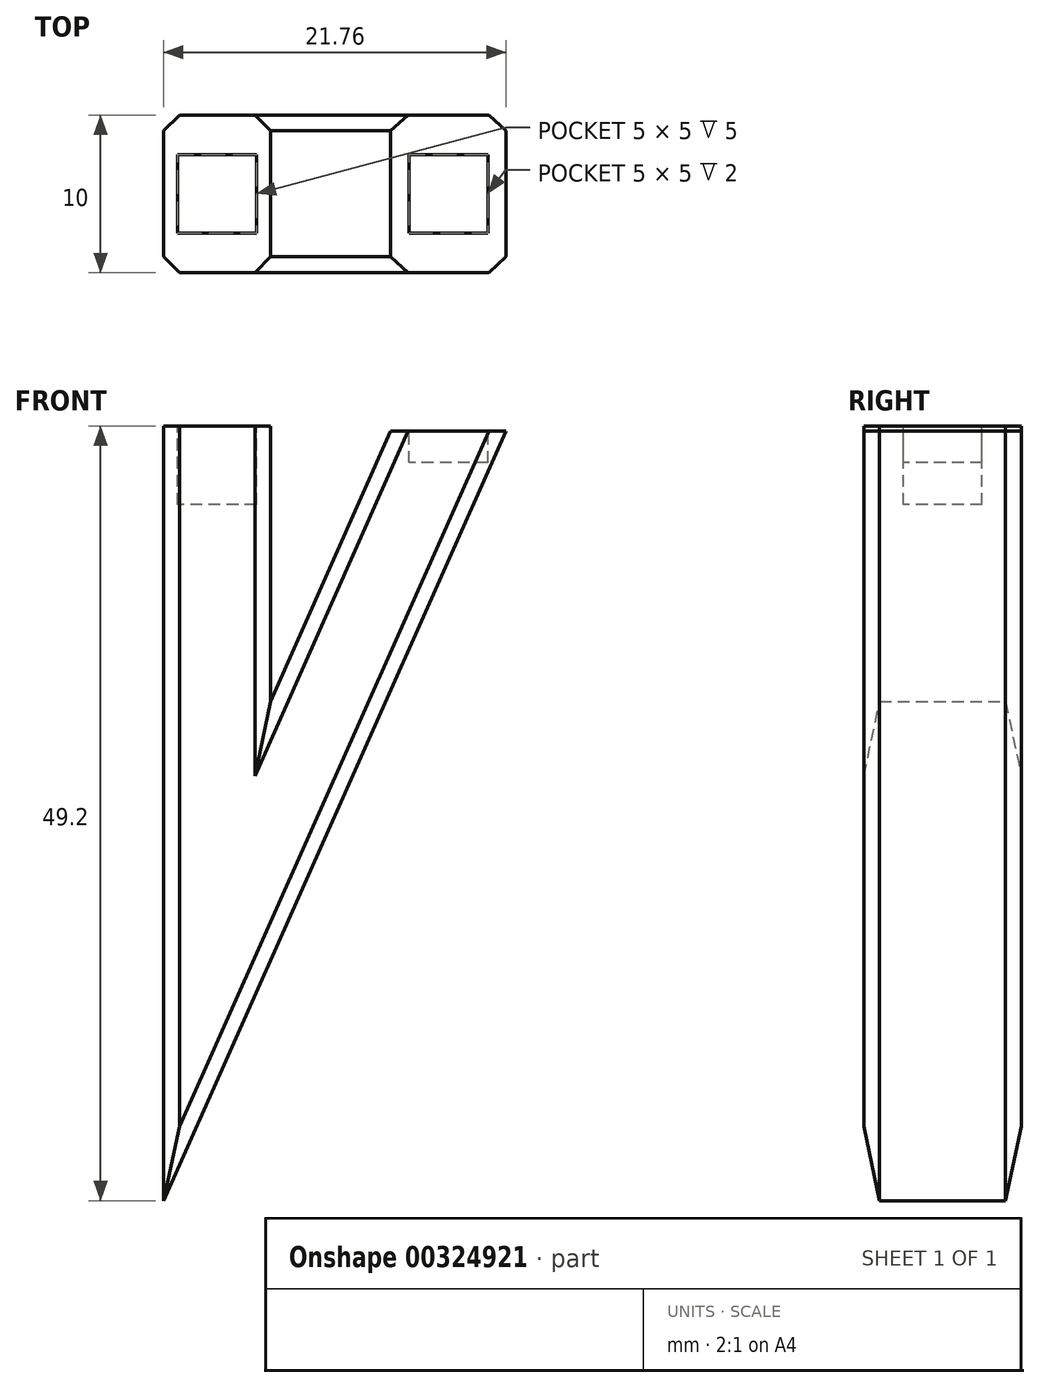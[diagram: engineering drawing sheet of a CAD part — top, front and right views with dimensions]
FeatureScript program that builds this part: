
annotation { "Feature Type Name" : "Feature", "Feature Type Description" : "" }
export const myFeature = defineFeature(function(context is Context, id is Id, definition is map)
    precondition{}
    {
        {
            var Q0;
            Q0=qCreatedBy(makeId("Front.planeOp"),FACE);
            var sketch = newSketch(context, id + "F0", { "sketchPlane" : qUnion([Q0])});
            skLineSegment(sketch, "E0", {"start": v(0, 0) * mm, "end": v(0, 49.2) * mm});
            skLineSegment(sketch, "E1", {"start": v(0, 0) * mm, "end": v(21.76, 48.87) * mm});
            skLineSegment(sketch, "E2", {"start": v(0, 49.2) * mm, "end": v(6.8, 49.2) * mm});
            skLineSegment(sketch, "E3", {"start": v(21.76, 48.87) * mm, "end": v(14.42, 48.87) * mm});
            skLineSegment(sketch, "E4", {"start": v(6.8, 49.2) * mm, "end": v(6.8, 31.7) * mm});
            skLineSegment(sketch, "E5", {"start": v(14.42, 48.87) * mm, "end": v(6.8, 31.7) * mm});
            skSolve(sketch);
        }
        {
            var Q0;
            Q0=makeQuery(id+"F0.imprint","IMPRINT",FACE,{"disambiguationData":[TD([[makeQuery(id+"F0.imprint","IMPRINT",EDGE,{"derivedFrom":sQuery(id+"F0.wireOp",EDGE,"E0")}),-1.0]])]});
            extrude(context, id + "F1", {"entities" : qUnion([Q0]), "depth" : 10 * mm});
        }
        {
            var Q0;
            Q0=makeQuery(id+"F1.opExtrude","SWEPT_FACE",FACE,{"disambiguationData":[OSD([sQuery(id+"F0.wireOp",EDGE,"E2")])]});
            var sketch = newSketch(context, id + "F2", { "sketchPlane" : qUnion([Q0])});
            skLineSegment(sketch, "E6.bottom", {"start": v(5.9, -2.5) * mm, "end": v(0.9, -2.5) * mm});
            skLineSegment(sketch, "E6.top", {"start": v(5.9, -7.5) * mm, "end": v(0.9, -7.5) * mm});
            skLineSegment(sketch, "E6.left", {"start": v(5.9, -2.5) * mm, "end": v(5.9, -7.5) * mm});
            skLineSegment(sketch, "E6.right", {"start": v(0.9, -2.5) * mm, "end": v(0.9, -7.5) * mm});
            skPoint(sketch, "E6.middle", {"position": v(3.4, -5) * mm});
            skSolve(sketch);
        }
        {
            var Q0;
            Q0=makeQuery(id+"F2.imprint","IMPRINT",FACE,{"disambiguationData":[TD([[makeQuery(id+"F2.imprint","IMPRINT",EDGE,{"derivedFrom":sQuery(id+"F2.wireOp",EDGE,"E6.bottom")}),1.0]])]});
            extrude(context, id + "F3", {"entities" : qUnion([Q0]), "operationType" : NewBodyOperationType.REMOVE, "oppositeDirection" : true, "depth" : 5 * mm});
        }
        {
            var Q0;
            Q0=makeQuery(id+"F1.opExtrude","SWEPT_FACE",FACE,{"disambiguationData":[OSD([sQuery(id+"F0.wireOp",EDGE,"E3")])]});
            var sketch = newSketch(context, id + "F4", { "sketchPlane" : qUnion([Q0])});
            skLineSegment(sketch, "E7.bottom", {"start": v(20.6, -2.5) * mm, "end": v(15.6, -2.5) * mm});
            skLineSegment(sketch, "E7.top", {"start": v(20.6, -7.5) * mm, "end": v(15.6, -7.5) * mm});
            skLineSegment(sketch, "E7.left", {"start": v(20.6, -2.5) * mm, "end": v(20.6, -7.5) * mm});
            skLineSegment(sketch, "E7.right", {"start": v(15.6, -2.5) * mm, "end": v(15.6, -7.5) * mm});
            skPoint(sketch, "E7.middle", {"position": v(18.1, -5) * mm});
            skSolve(sketch);
        }
        {
            var Q0;
            Q0=makeQuery(id+"F4.imprint","IMPRINT",FACE,{"disambiguationData":[TD([[makeQuery(id+"F4.imprint","IMPRINT",EDGE,{"derivedFrom":sQuery(id+"F4.wireOp",EDGE,"E7.bottom")}),1.0]])]});
            extrude(context, id + "F5", {"entities" : qUnion([Q0]), "operationType" : NewBodyOperationType.REMOVE, "oppositeDirection" : true, "depth" : 2 * mm});
        }
        {
            var Q0;
            Q0=makeQuery(id+"F1.opExtrude","CAP_EDGE",EDGE,{"disambiguationData":[OSD([sQuery(id+"F0.wireOp",EDGE,"E4")])],"isStart":false});
            var Q1;
            Q1=makeQuery(id+"F1.opExtrude","CAP_EDGE",EDGE,{"disambiguationData":[OSD([sQuery(id+"F0.wireOp",EDGE,"E0")])],"isStart":false});
            var Q2;
            Q2=makeQuery(id+"F1.opExtrude","CAP_EDGE",EDGE,{"disambiguationData":[OSD([sQuery(id+"F0.wireOp",EDGE,"E5")])],"isStart":false});
            var Q3;
            Q3=makeQuery(id+"F1.opExtrude","CAP_EDGE",EDGE,{"disambiguationData":[OSD([sQuery(id+"F0.wireOp",EDGE,"E4")])],"isStart":true});
            var Q4;
            Q4=makeQuery(id+"F1.opExtrude","CAP_EDGE",EDGE,{"disambiguationData":[OSD([sQuery(id+"F0.wireOp",EDGE,"E1")])],"isStart":true});
            var Q5;
            Q5=makeQuery(id+"F1.opExtrude","CAP_EDGE",EDGE,{"disambiguationData":[OSD([sQuery(id+"F0.wireOp",EDGE,"E5")])],"isStart":true});
            var Q6;
            Q6=makeQuery(id+"F1.opExtrude","CAP_EDGE",EDGE,{"disambiguationData":[OSD([sQuery(id+"F0.wireOp",EDGE,"E1")])],"isStart":false});
            var Q7;
            Q7=makeQuery(id+"F1.opExtrude","CAP_EDGE",EDGE,{"disambiguationData":[OSD([sQuery(id+"F0.wireOp",EDGE,"E0")])],"isStart":true});
            chamfer(context, id + "F6", {"entities" : qUnion([Q0, Q1, Q2, Q3, Q4, Q5, Q6, Q7]), "width" : 1 * mm, "tangentPropagation" : true});
        }
    });
